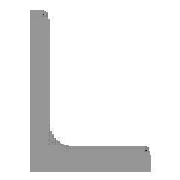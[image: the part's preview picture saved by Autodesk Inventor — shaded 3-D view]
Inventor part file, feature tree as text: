
AUTODESK INVENTOR PART (.ipt)
format: ipt  version: 2024.1 (Build 281209000, 209)  size: 132,608 bytes
history: native  units: mm (DEFAULTED — no unit token found)
features: other x4, plane x3, split x2, sketch x1
ambient origin geometry x8: Origin, YZ Plane, XZ Plane, XY Plane, X Axis, Y Axis, Z Axis, Center Point
bodies: Solid1 (feature_tree), Body (feature_tree)
feature tree (10):
  parser-record x1  (decoder bookkeeping rows leaked as tree rows — omitted from the tree; the rows remain in map.json)
  other  "Driven Length"
  other  "Start Plane"
  other  "End Plane"
  plane  "Work Plane4"
  split  "Split1"
  plane  "Work Plane5"
  split  "Split2"
  sketch  "Sketch3"  dims[d0=25.4mm d1=25.4mm d2=3.175mm d3=3.175mm d4=625.4mm d5=0.0mm d10=0.0mm d11=0.0mm d12=-12.7mm d13=612.7mm d14=3.302mm d15=1.524mm d16=90.0deg d17=625.4mm]
  plane  "Work Plane3"
